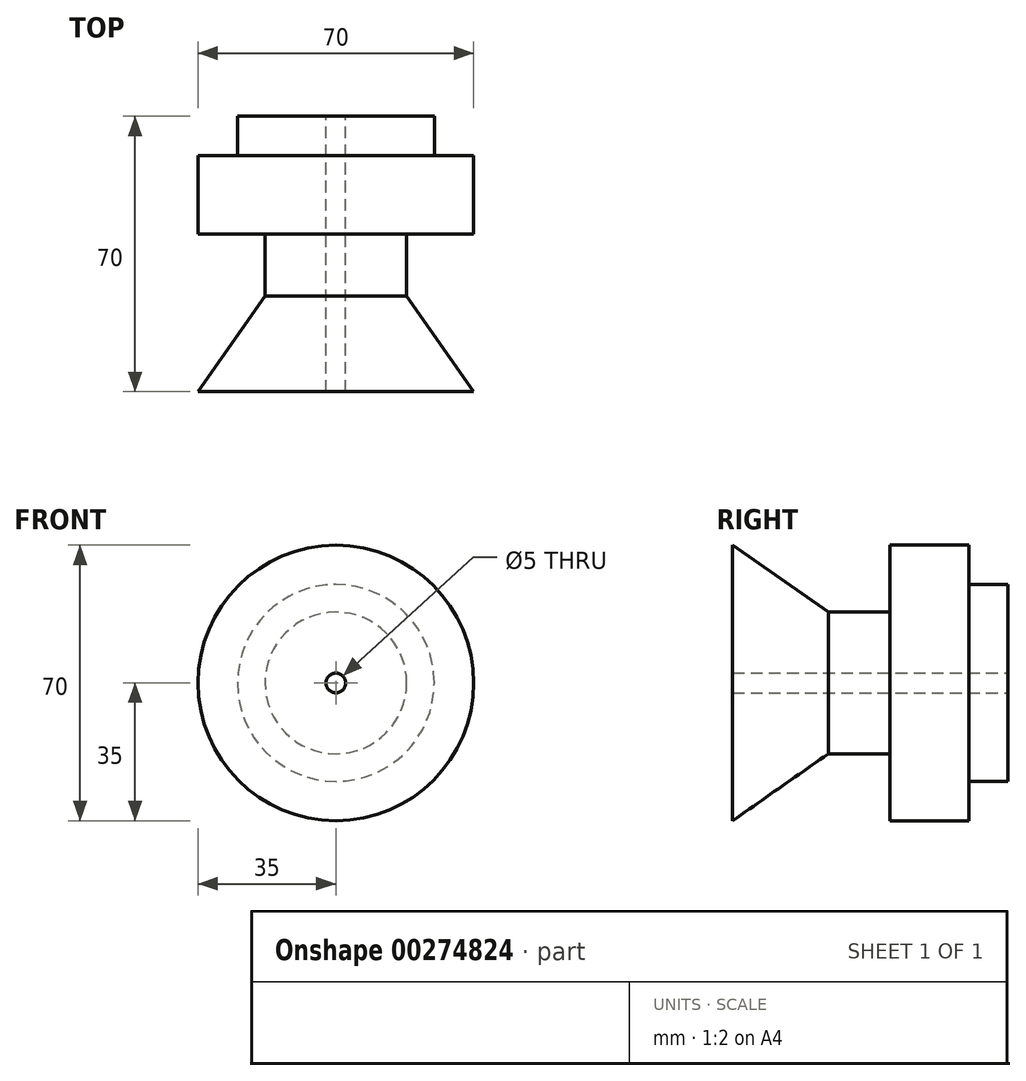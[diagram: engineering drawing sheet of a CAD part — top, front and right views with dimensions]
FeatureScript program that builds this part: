
annotation { "Feature Type Name" : "Feature", "Feature Type Description" : "" }
export const myFeature = defineFeature(function(context is Context, id is Id, definition is map)
    precondition{}
    {
        {
            var Q0;
            Q0=qCreatedBy(makeId("Top.planeOp"),FACE);
            var sketch = newSketch(context, id + "F0", { "sketchPlane" : qUnion([Q0])});
            skLineSegment(sketch, "E0.left", {"start": v(0, 0) * mm, "end": v(0, 40) * mm});
            skLineSegment(sketch, "E1.left", {"start": v(0, 0) * mm, "end": v(0, -30) * mm});
            skLineSegment(sketch, "E2", {"start": v(-35, -30) * mm, "end": v(-18, -5.72) * mm});
            skLineSegment(sketch, "E3", {"start": v(0, -30) * mm, "end": v(-35, -30) * mm});
            skLineSegment(sketch, "E4", {"start": v(0, 40) * mm, "end": v(-25, 40) * mm});
            skLineSegment(sketch, "E5", {"start": v(-25, 40) * mm, "end": v(-25, 30) * mm});
            skLineSegment(sketch, "E6", {"start": v(-25, 30) * mm, "end": v(-35, 30) * mm});
            skLineSegment(sketch, "E7", {"start": v(-35, 30) * mm, "end": v(-35, 10) * mm});
            skLineSegment(sketch, "E8", {"start": v(-35, 10) * mm, "end": v(-18, 10) * mm});
            skLineSegment(sketch, "E9", {"start": v(-18, 10) * mm, "end": v(-18, -5.72) * mm});
            skSolve(sketch);
        }
        {
            var Q0;
            Q0=makeQuery(id+"F0.imprint","IMPRINT",FACE,{"disambiguationData":[TD([[makeQuery(id+"F0.imprint","IMPRINT",EDGE,{"derivedFrom":sQuery(id+"F0.wireOp",EDGE,"E0.left")}),1.0]])]});
            var Q1;
            Q1=sQuery(id+"F0.wireOp",EDGE,"E0.left");
            revolve(context, id + "F1", {"entities" : qUnion([Q0]), "axis" : qUnion([Q1]), "revolveType" : RevolveType.FULL});
        }
        {
            var Q0;
            Q0=makeQuery(id+"F1.opRevolve","SWEPT_FACE",FACE,{"disambiguationData":[OSD([sQuery(id+"F0.wireOp",EDGE,"E4")])]});
            var sketch = newSketch(context, id + "F2", { "sketchPlane" : qUnion([Q0])});
            skCircle(sketch, "E10", {"center": v(0, 0) * mm, "radius": 2.5 * mm});
            skSolve(sketch);
        }
        {
            var Q0;
            Q0=makeQuery(id+"F2.imprint","IMPRINT",FACE,{"disambiguationData":[TD([[makeQuery(id+"F2.imprint","IMPRINT",EDGE,{"derivedFrom":sQuery(id+"F2.wireOp",EDGE,"E10")}),1.0]])]});
            extrude(context, id + "F3", {"entities" : qUnion([Q0]), "operationType" : NewBodyOperationType.REMOVE, "endBound" : BoundingType.THROUGH_ALL, "oppositeDirection" : true, "depth" : 10 * mm});
        }
    });
